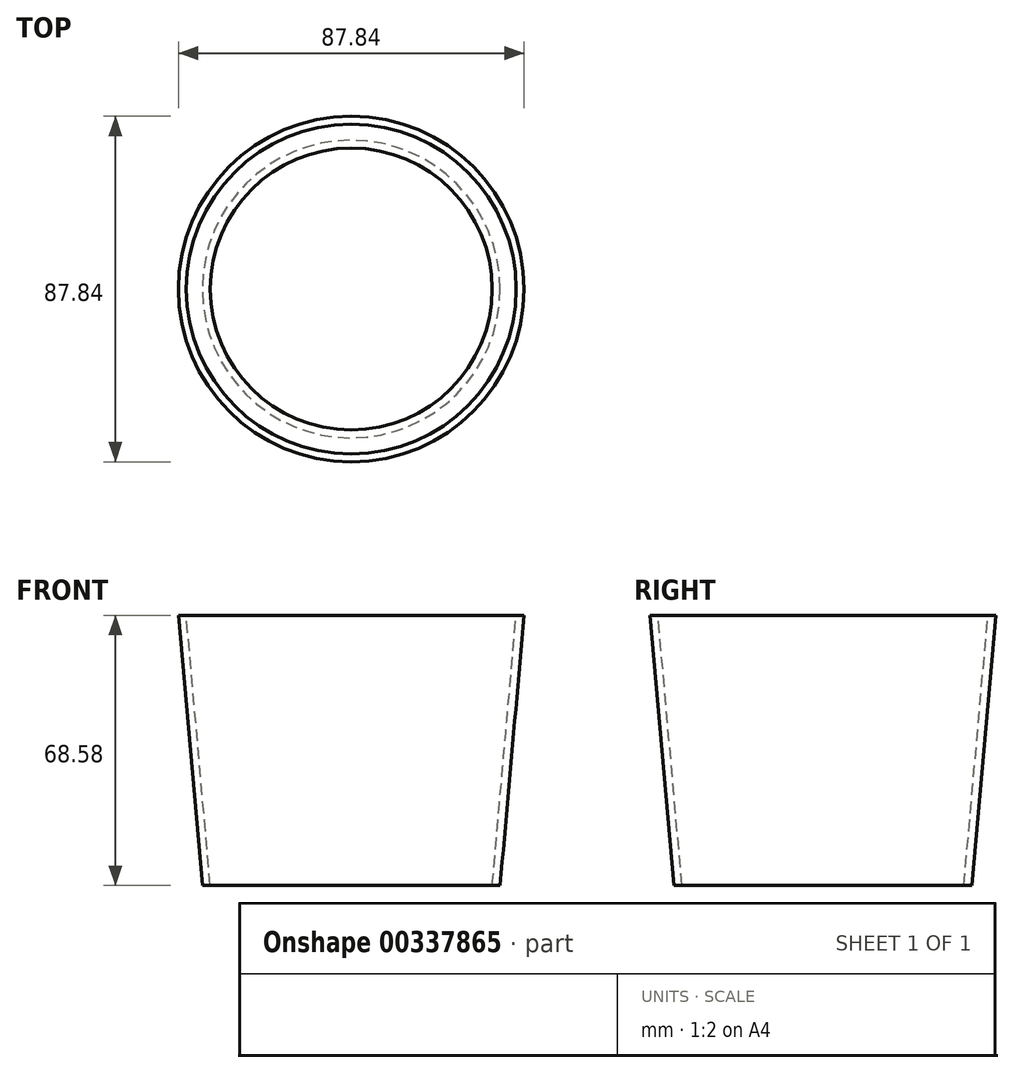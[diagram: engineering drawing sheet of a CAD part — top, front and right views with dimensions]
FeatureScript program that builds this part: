
annotation { "Feature Type Name" : "Feature", "Feature Type Description" : "" }
export const myFeature = defineFeature(function(context is Context, id is Id, definition is map)
    precondition{}
    {
        {
            var Q0;
            Q0=qCreatedBy(makeId("Front.planeOp"),FACE);
            var sketch = newSketch(context, id + "F0", { "sketchPlane" : qUnion([Q0])});
            skLineSegment(sketch, "E0", {"start": v(-41.91, 27.84) * mm, "end": v(-35.81, -40.74) * mm});
            skLineSegment(sketch, "E1", {"start": v(-35.81, -40.74) * mm, "end": v(0, -40.74) * mm, "construction": true});
            skLineSegment(sketch, "E2", {"start": v(-41.91, 27.84) * mm, "end": v(0, 27.84) * mm, "construction": true});
            skLineSegment(sketch, "E3", {"start": v(0, 27.84) * mm, "end": v(0, -40.74) * mm, "construction": true});
            skLineSegment(sketch, "E4.0", {"start": v(-43.92, 27.84) * mm, "end": v(-37.82, -40.74) * mm});
            skLineSegment(sketch, "E5", {"start": v(-41.91, 27.84) * mm, "end": v(-43.92, 27.84) * mm});
            skLineSegment(sketch, "E6", {"start": v(-35.81, -40.74) * mm, "end": v(-37.82, -40.74) * mm});
            skSolve(sketch);
        }
        {
            var Q0;
            Q0=makeQuery(id+"F0.imprint","IMPRINT",FACE,{"disambiguationData":[TD([[makeQuery(id+"F0.imprint","IMPRINT",EDGE,{"derivedFrom":sQuery(id+"F0.wireOp",EDGE,"E0")}),-1.0]])]});
            var Q1;
            Q1=sQuery(id+"F0.wireOp",EDGE,"E3");
            revolve(context, id + "F1", {"entities" : qUnion([Q0]), "axis" : qUnion([Q1]), "revolveType" : RevolveType.FULL});
        }
    });
